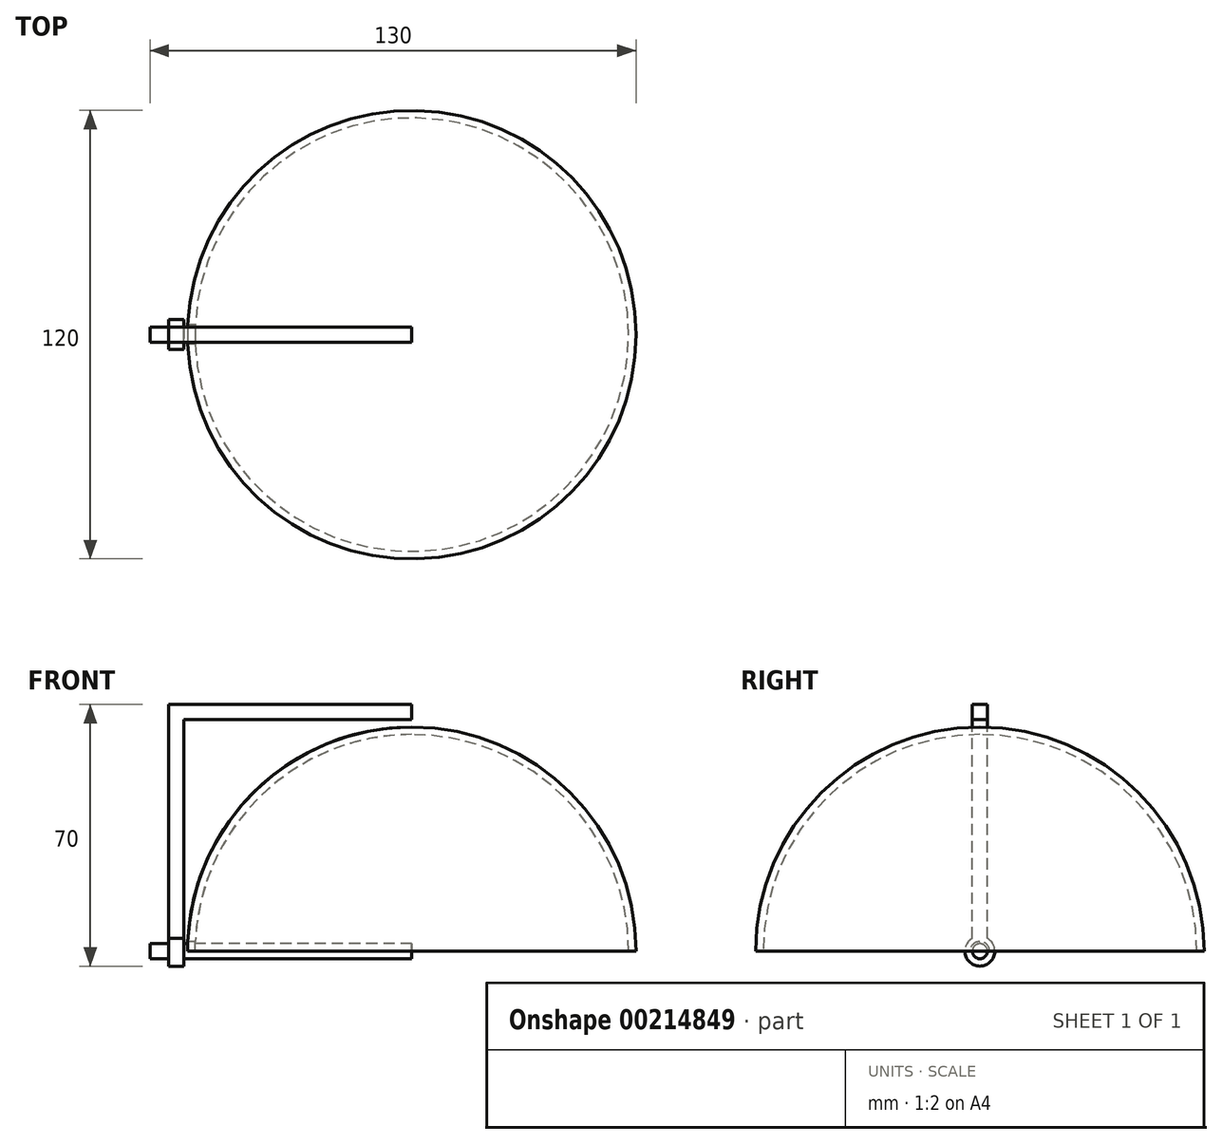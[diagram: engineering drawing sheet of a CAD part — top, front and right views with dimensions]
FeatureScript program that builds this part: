
annotation { "Feature Type Name" : "Feature", "Feature Type Description" : "" }
export const myFeature = defineFeature(function(context is Context, id is Id, definition is map)
    precondition{}
    {
        {
            var Q0;
            Q0=qCreatedBy(makeId("Front.planeOp"),FACE);
            var sketch = newSketch(context, id + "F0", { "sketchPlane" : qUnion([Q0])});
            skArc(sketch, "E0", {"start": v(0, 60) * mm, "mid": v(-42.43, 42.43) * mm, "end": v(-60, 0) * mm});
            skLineSegment(sketch, "E1", {"start": v(0, 0) * mm, "end": v(0, 60) * mm});
            skLineSegment(sketch, "E2", {"start": v(0, 0) * mm, "end": v(-60, 0) * mm});
            skArc(sketch, "E3", {"start": v(0, 58) * mm, "mid": v(-41.01, 41.01) * mm, "end": v(-58, 0) * mm});
            skSolve(sketch);
        }
        {
            var Q0;
            Q0=qCreatedBy(makeId("Front.planeOp"),FACE);
            var sketch = newSketch(context, id + "F1", { "sketchPlane" : qUnion([Q0])});
            skArc(sketch, "E4.0", {"start": v(0, 58) * mm, "mid": v(-41.01, 41.01) * mm, "end": v(-58, 0) * mm, "construction": true});
            skArc(sketch, "E5.0", {"start": v(0, 60) * mm, "mid": v(-42.43, 42.43) * mm, "end": v(-60, 0) * mm, "construction": true});
            skLineSegment(sketch, "E6", {"start": v(0, 2) * mm, "end": v(-70, 2) * mm});
            skLineSegment(sketch, "E7", {"start": v(-70, 2) * mm, "end": v(-70, 0) * mm});
            skLineSegment(sketch, "E8", {"start": v(-70, 0) * mm, "end": v(0, 0) * mm});
            skLineSegment(sketch, "E9", {"start": v(0, 2) * mm, "end": v(0, 0) * mm});
            skLineSegment(sketch, "E10", {"start": v(0, 2) * mm, "end": v(0, 2.6) * mm});
            skLineSegment(sketch, "E11", {"start": v(0, 2.6) * mm, "end": v(-70, 2.6) * mm});
            skLineSegment(sketch, "E12", {"start": v(-70, 2.6) * mm, "end": v(-70, 2) * mm});
            skSolve(sketch);
        }
        {
            var Q0;
            Q0=qCreatedBy(makeId("Front.planeOp"),FACE);
            var sketch = newSketch(context, id + "F2", { "sketchPlane" : qUnion([Q0])});
            skLineSegment(sketch, "E13.0.0", {"start": v(0, 0) * mm, "end": v(0, 2) * mm});
            skLineSegment(sketch, "E13.0.1", {"start": v(0, 2) * mm, "end": v(-70, 2) * mm});
            skLineSegment(sketch, "E13.0.2", {"start": v(-70, 2) * mm, "end": v(-70, 0) * mm});
            skLineSegment(sketch, "E13.0.3", {"start": v(-70, 0) * mm, "end": v(0, 0) * mm});
            skLineSegment(sketch, "E14", {"start": v(-65, 2) * mm, "end": v(-65, 4) * mm});
            skLineSegment(sketch, "E15", {"start": v(-65, 4) * mm, "end": v(-61, 4) * mm});
            skLineSegment(sketch, "E16", {"start": v(-61, 4) * mm, "end": v(-61, 2) * mm});
            skLineSegment(sketch, "E17", {"start": v(-65, 4) * mm, "end": v(-65, 62) * mm});
            skLineSegment(sketch, "E18", {"start": v(-61, 4) * mm, "end": v(-61, 62) * mm});
            skLineSegment(sketch, "E19", {"start": v(-61, 62) * mm, "end": v(-65, 62) * mm});
            skLineSegment(sketch, "E20", {"start": v(-61, 62) * mm, "end": v(0, 62) * mm});
            skLineSegment(sketch, "E21", {"start": v(0, 62) * mm, "end": v(0, 66) * mm});
            skLineSegment(sketch, "E22", {"start": v(0, 66) * mm, "end": v(-65, 66) * mm});
            skLineSegment(sketch, "E23", {"start": v(-65, 66) * mm, "end": v(-65, 62) * mm});
            skSolve(sketch);
        }
        {
            var Q0;
            {var subQ0=sQuery(id+"F0.wireOp",EDGE,"E0");Q0=makeQuery(id+"F0.imprint","IMPRINT",FACE,{"disambiguationData":[TD([[makeQuery(id+"F0.imprint","IMPRINT",EDGE,{"derivedFrom":subQ0}),1.0]])]});}
            var Q1;
            Q1=sQuery(id+"F0.wireOp",EDGE,"E1");
            revolve(context, id + "F3", {"entities" : qUnion([Q0]), "axis" : qUnion([Q1]), "revolveType" : RevolveType.FULL});
        }
        {
            var Q0;
            Q0=makeQuery(id+"F1.imprint","IMPRINT",FACE,{"disambiguationData":[TD([[makeQuery(id+"F1.imprint","IMPRINT",EDGE,{"derivedFrom":sQuery(id+"F1.wireOp",EDGE,"E6")}),1.0]])]});
            var Q1;
            Q1=sQuery(id+"F1.wireOp",EDGE,"E8");
            revolve(context, id + "F4", {"operationType" : NewBodyOperationType.ADD, "entities" : qUnion([Q0]), "axis" : qUnion([Q1]), "revolveType" : RevolveType.FULL});
        }
        {
            var Q0;
            Q0=makeQuery(id+"F1.imprint","IMPRINT",FACE,{"disambiguationData":[TD([[makeQuery(id+"F1.imprint","IMPRINT",EDGE,{"derivedFrom":sQuery(id+"F1.wireOp",EDGE,"E6")}),-1.0]])]});
            var Q1;
            Q1=sQuery(id+"F0.wireOp",EDGE,"E2");
            revolve(context, id + "F5", {"operationType" : NewBodyOperationType.REMOVE, "entities" : qUnion([Q0]), "axis" : qUnion([Q1]), "revolveType" : RevolveType.FULL, "oppositeDirection" : true});
        }
        {
            var Q0;
            {var subQ0=sQuery(id+"F2.wireOp",EDGE,"E14");Q0=makeQuery(id+"F2.imprint","IMPRINT",FACE,{"disambiguationData":[TD([[makeQuery(id+"F2.imprint","IMPRINT",EDGE,{"derivedFrom":subQ0}),-1.0]])]});}
            var Q1;
            Q1=sQuery(id+"F0.wireOp",EDGE,"E2");
            revolve(context, id + "F6", {"entities" : qUnion([Q0]), "axis" : qUnion([Q1]), "revolveType" : RevolveType.FULL});
        }
        {
            var Q0;
            Q0=makeQuery(id+"F2.imprint","IMPRINT",FACE,{"disambiguationData":[TD([[makeQuery(id+"F2.imprint","IMPRINT",EDGE,{"derivedFrom":sQuery(id+"F2.wireOp",EDGE,"E15")}),1.0]])]});
            var Q1;
            Q1=makeQuery(id+"F2.imprint","IMPRINT",FACE,{"disambiguationData":[TD([[makeQuery(id+"F2.imprint","IMPRINT",EDGE,{"derivedFrom":sQuery(id+"F2.wireOp",EDGE,"E19")}),-1.0]])]});
            var Q2;
            {var subQ0=sQuery(id+"F2.wireOp",EDGE,"E14");Q2=makeQuery(id+"F2.imprint","IMPRINT",FACE,{"disambiguationData":[TD([[makeQuery(id+"F2.imprint","IMPRINT",EDGE,{"derivedFrom":subQ0}),-1.0]])]});}
            extrude(context, id + "F7", {"entities" : qUnion([Q0, Q1, Q2]), "operationType" : NewBodyOperationType.ADD, "depth" : 2 * mm, "hasSecondDirection" : true, "secondDirectionOppositeDirection" : true, "secondDirectionDepth" : 2 * mm});
        }
    });
